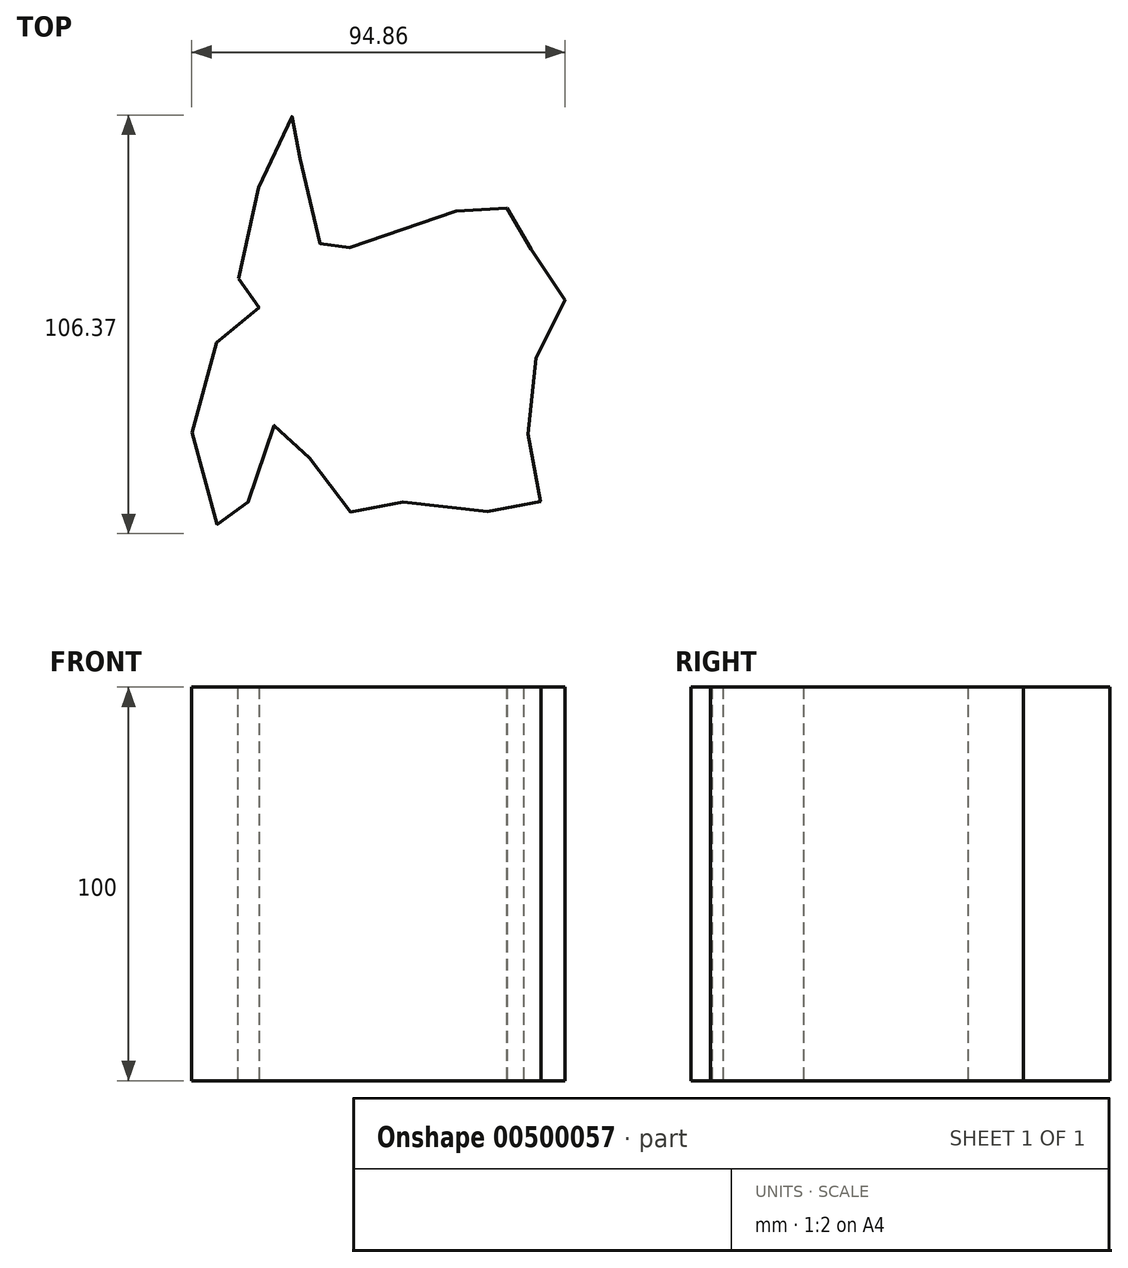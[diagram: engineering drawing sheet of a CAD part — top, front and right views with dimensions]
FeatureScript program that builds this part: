
annotation { "Feature Type Name" : "Feature", "Feature Type Description" : "" }
export const myFeature = defineFeature(function(context is Context, id is Id, definition is map)
    precondition{}
    {
        {
            var Q0;
            Q0=qCreatedBy(makeId("Top.planeOp"),FACE);
            var sketch = newSketch(context, id + "F0", { "sketchPlane" : qUnion([Q0])});
            skFitSpline(sketch, "E0", {"points": [v(-56.84, 9.47) * mm, v(-43.14, 50.86) * mm, v(-42.85, 49.11) * mm, v(-35.56, 15.3) * mm, v(-35.27, 15.01) * mm, v(10.5, 29) * mm, v(11.37, 24.34) * mm, v(25.94, 5.98) * mm, v(15.74, -19.38) * mm, v(18.95, -48.82) * mm, v(-14.87, -47.36) * mm, v(-30.9, -48.53) * mm, v(-46.64, -26.96) * mm, v(-58.59, -55.23) * mm, v(-67.04, -14.43) * mm, v(-51.6, 2.48) * mm, v(-56.84, 9.47) * mm]});
            skSolve(sketch);
        }
        {
            var Q0;
            Q0 = qSketchRegion(id + "F0", true);
            extrude(context, id + "F1", {"entities" : qUnion([Q0]), "depth" : 100 * mm});
        }
    });
